# Revit family: Veko Highlight Spot
name_source: partatom
category: Lighting Fixtures
revit_build: Autodesk Revit 2017 (Build: 20190508_0315(x64)
units: mm (PartAtom-declared; Revit-internal decimal feet)

## family parameters
Always vertical = No
Cut with Voids When Loaded = No
Light Source = No
Part Type = Normal
Room Calculation Point = No
Round Connector Dimension = Use Diameter
Shared = No
Work Plane-Based = Yes

## types (2) — shared parameters
Apparent Load = 35 VA
Article Number = On Request
Assembly Code = 63.00
Default Elevation = 1219 mm
Description = Veko Highlight Spot
IK Value = IK02
IP Value = IP20
IfcExportAs = IfcLightFixtureType
IfcExportType = POINTSOURCE
Lamp = LED
Manufacturer = Veko Lightsystems
URL = https://www.veko.com

## per-type parameters (varying)
| type | ColorTemperature | Model |
| 3000K | LightLine_Spot_Rotation : 3000K | 3000K Spot |
| 4000K | LightLine_Spot_Rotation : 4000K | 4000K Spot |

## geometry (parser evidence)
native form markers: Sweep x17
no freeform markers — native parametric forms only
